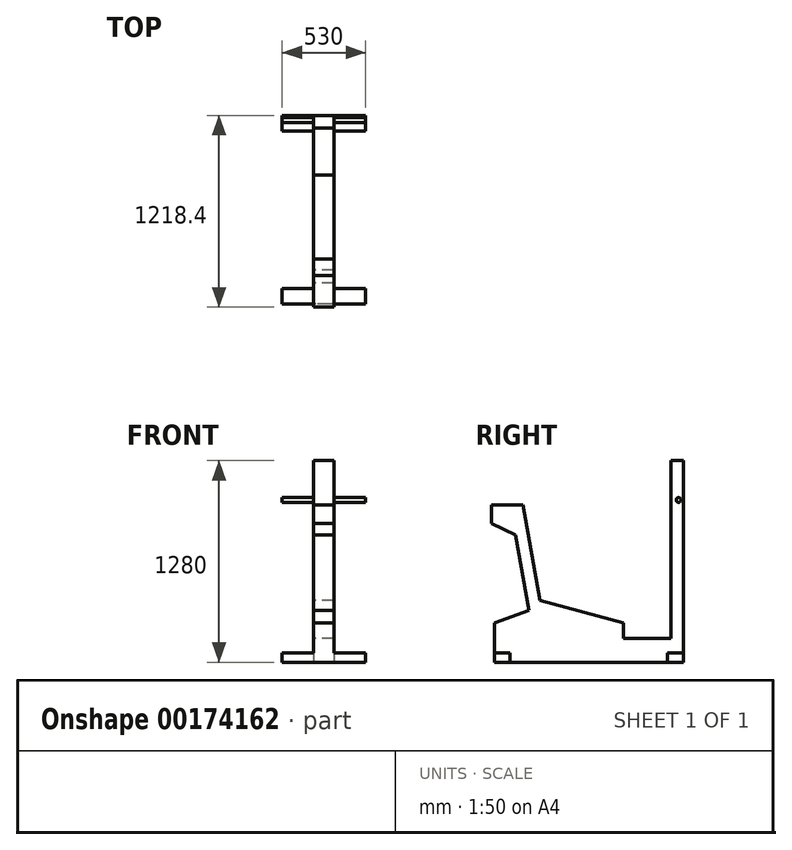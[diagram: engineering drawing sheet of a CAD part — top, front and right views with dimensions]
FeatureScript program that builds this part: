
annotation { "Feature Type Name" : "Feature", "Feature Type Description" : "" }
export const myFeature = defineFeature(function(context is Context, id is Id, definition is map)
    precondition{}
    {
        {
            var Q0;
            Q0=qCreatedBy(makeId("Right.planeOp"),FACE);
            var sketch = newSketch(context, id + "F0", { "sketchPlane" : qUnion([Q0])});
            skLineSegment(sketch, "E0", {"start": v(0, 0) * mm, "end": v(1200, 0) * mm});
            skLineSegment(sketch, "E1", {"start": v(1200, 0) * mm, "end": v(1200, 1280) * mm});
            skLineSegment(sketch, "E2", {"start": v(1200, 1280) * mm, "end": v(1120, 1280) * mm});
            skLineSegment(sketch, "E3", {"start": v(1120, 1280) * mm, "end": v(1120, 150) * mm});
            skLineSegment(sketch, "E4", {"start": v(1120, 150) * mm, "end": v(820, 150) * mm});
            skLineSegment(sketch, "E5", {"start": v(820, 150) * mm, "end": v(820, 250) * mm});
            skLineSegment(sketch, "E6", {"start": v(820, 250) * mm, "end": v(288.74, 392.35) * mm});
            skLineSegment(sketch, "E7", {"start": v(288.74, 392.35) * mm, "end": v(181.6, 1000) * mm});
            skLineSegment(sketch, "E8", {"start": v(181.6, 1000) * mm, "end": v(-18.4, 1000) * mm});
            skLineSegment(sketch, "E9", {"start": v(-18.4, 1000) * mm, "end": v(-18.4, 880) * mm});
            skLineSegment(sketch, "E10", {"start": v(-18.4, 880) * mm, "end": v(134.06, 808.9) * mm});
            skLineSegment(sketch, "E11", {"start": v(134.06, 808.9) * mm, "end": v(218.58, 329.56) * mm});
            skLineSegment(sketch, "E12", {"start": v(218.58, 329.56) * mm, "end": v(0, 250) * mm});
            skLineSegment(sketch, "E13", {"start": v(0, 250) * mm, "end": v(0, 0) * mm});
            skSolve(sketch);
        }
        {
            var Q0;
            Q0=makeQuery(id+"F0.imprint","IMPRINT",FACE,{"disambiguationData":[TD([[makeQuery(id+"F0.imprint","IMPRINT",EDGE,{"derivedFrom":sQuery(id+"F0.wireOp",EDGE,"E0")}),1.0]])]});
            extrude(context, id + "F1", {"entities" : qUnion([Q0]), "endBound" : BoundingType.SYMMETRIC, "depth" : 130 * mm});
        }
        {
            var Q0;
            Q0=qCreatedBy(makeId("Right.planeOp"),FACE);
            var sketch = newSketch(context, id + "F2", { "sketchPlane" : qUnion([Q0])});
            skLineSegment(sketch, "E14", {"start": v(600, 0) * mm, "end": v(600, -146.73) * mm, "construction": true});
            skLineSegment(sketch, "E15.bottom", {"start": v(0, 0) * mm, "end": v(100, 0) * mm});
            skLineSegment(sketch, "E15.top", {"start": v(0, 60) * mm, "end": v(100, 60) * mm});
            skLineSegment(sketch, "E15.left", {"start": v(0, 0) * mm, "end": v(0, 60) * mm});
            skLineSegment(sketch, "E15.right", {"start": v(100, 0) * mm, "end": v(100, 60) * mm});
            skLineSegment(sketch, "E16.MirrorCS", {"start": v(1100, 0) * mm, "end": v(1100, 60) * mm});
            skLineSegment(sketch, "E17.MirrorCS", {"start": v(1200, 60) * mm, "end": v(1100, 60) * mm});
            skLineSegment(sketch, "E18.MirrorCS", {"start": v(1200, 0) * mm, "end": v(1200, 60) * mm});
            skLineSegment(sketch, "E19.MirrorCS", {"start": v(1200, 0) * mm, "end": v(1100, 0) * mm});
            skSolve(sketch);
        }
        {
            var Q0;
            Q0=qSketchRegion(id+"F2",true);
            extrude(context, id + "F3", {"entities" : qUnion([Q0]), "operationType" : NewBodyOperationType.ADD, "endBound" : BoundingType.SYMMETRIC, "depth" : 530 * mm});
        }
        {
            var Q0;
            Q0=qCreatedBy(makeId("Right.planeOp"),FACE);
            var sketch = newSketch(context, id + "F4", { "sketchPlane" : qUnion([Q0])});
            skCircle(sketch, "E20", {"center": v(1170, 1030) * mm, "radius": 15 * mm});
            skSolve(sketch);
        }
        {
            var Q0;
            Q0=qSketchRegion(id+"F4",true);
            extrude(context, id + "F5", {"entities" : qUnion([Q0]), "operationType" : NewBodyOperationType.ADD, "endBound" : BoundingType.SYMMETRIC, "depth" : 530 * mm});
        }
    });
